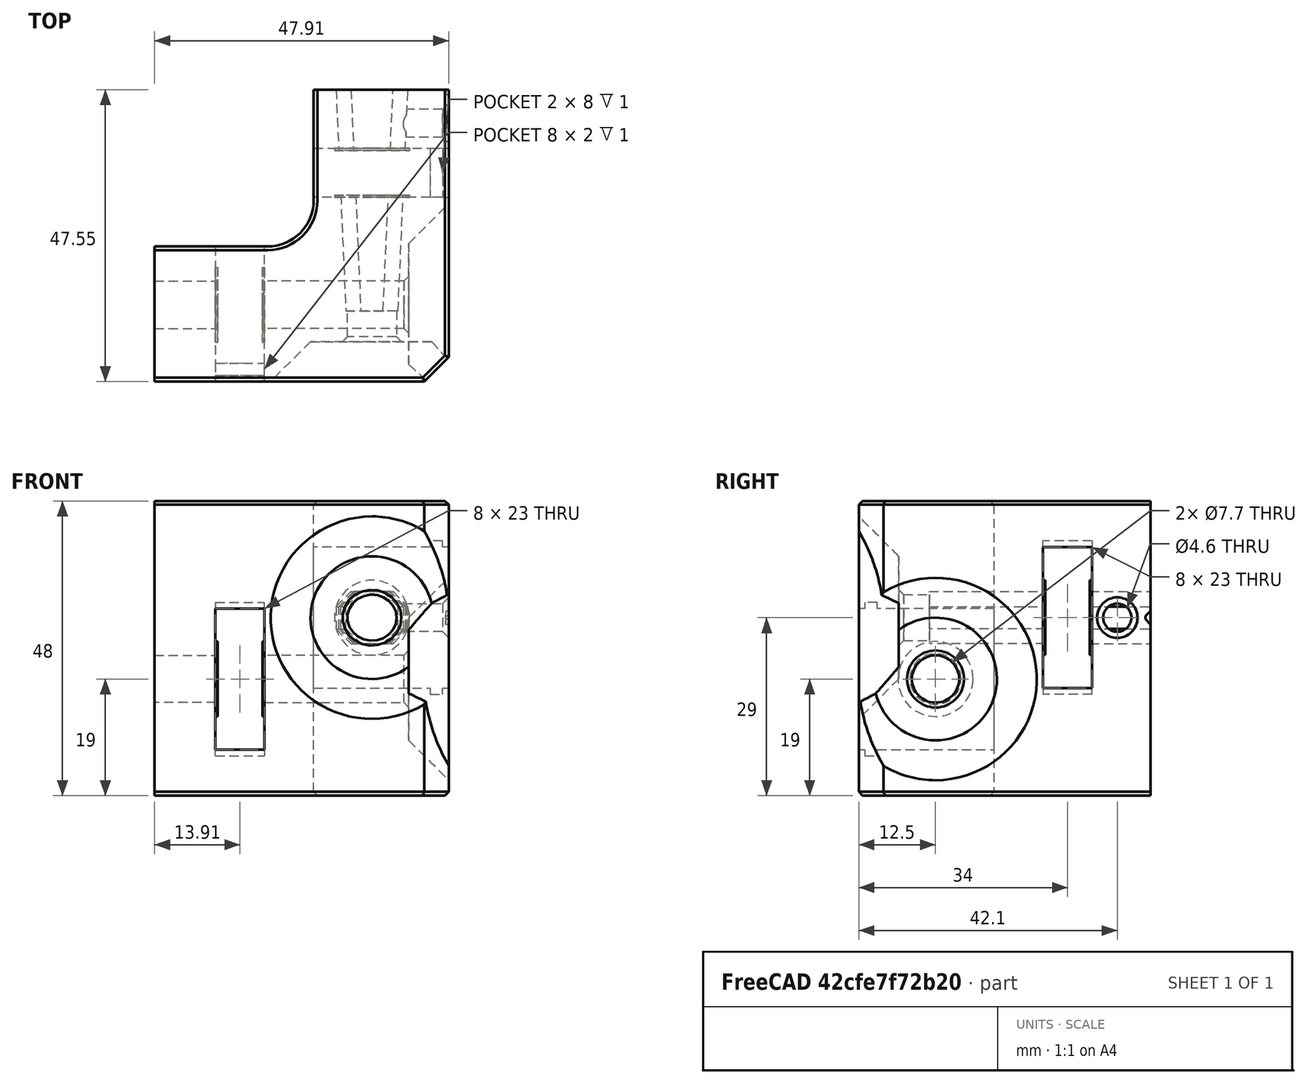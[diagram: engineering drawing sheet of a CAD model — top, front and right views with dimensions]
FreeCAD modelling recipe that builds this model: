
FCSTD DOCUMENT  (FreeCAD 1.0R38641 +678 (Git))
Label: Testpiece_from _60mmx40mm_tube_version
License: All rights reserved
LicenseURL: https://en.wikipedia.org/wiki/All_rights_reserved
objects: Part::Feature×1, PartDesign::FeatureBase×1, Sketcher::SketchObject×1, PartDesign::Pocket×1, PartDesign::Body×1
note: 9 computed .brp shape members not serialized (recipe doc carries the construction recipe); baked Part::Feature solids carry a one-line shape summary decoded from their .brp

FEATURE [Part::Feature] Cut003  label="Bearing ring - with all booleans001"
  shape: bbox 48 x 94.54 x 114.1 mm, 320 faces (baked)
FEATURE [PartDesign::FeatureBase] BaseFeature
  BaseFeature = -> Cut003
  Suppressed = false
FEATURE [Sketcher::SketchObject] Sketch
  ArcFitTolerance = 1e-06
  AttachmentSupport = -> [YZ_Plane]
  FullyConstrained = false
  MakeInternals = false
  MapMode = 5
  Placement = pos=(0,0,0) rot=(0.57735,0.57735,0.57735;2.0944rad)
  sketch-geometry (6):
    g0: LineSegment StartX=-52.603 StartY=-5.59485 StartZ=0 EndX=4.0497 EndY=-5.59485 EndZ=0
    g1: LineSegment StartX=4.0497 StartY=-5.59485 StartZ=0 EndX=4.0497 EndY=-63.1029 EndZ=0
    g2: LineSegment StartX=4.0497 StartY=-63.1029 StartZ=0 EndX=82.855 EndY=-63.1029 EndZ=0
    g3: LineSegment StartX=82.855 StartY=-63.1029 StartZ=0 EndX=76.1628 EndY=73.3227 EndZ=0
    g4: LineSegment StartX=76.1628 StartY=73.3227 StartZ=0 EndX=-61.6335 EndY=67.6786 EndZ=0
    g5: LineSegment StartX=-61.6335 StartY=67.6786 StartZ=0 EndX=-52.603 EndY=-5.59485 EndZ=0
  constraints (9):
    c: Horizontal(g0)
    c: Coincident(g0,g1)
    c: Vertical(g1)
    c: Coincident(g1,g2)
    c: Horizontal(g2)
    c: Coincident(g2,g3)
    c: Coincident(g3,g4)
    c: Coincident(g4,g5)
    c: Coincident(g5,g0)
FEATURE [PartDesign::Pocket] Pocket
  BaseFeature = -> BaseFeature
  Direction = (-1,0,0)
  Length = 5
  Length2 = 5
  Midplane = true
  Profile = -> Sketch
  ReferenceAxis = -> Sketch [N_Axis]
  Refine = true
  Suppressed = false
  Type = 1
FEATURE [PartDesign::Body] Body  label="Testpiece"
  AllowCompound = false
  BaseFeature = -> Cut003
  Group = -> [BaseFeature,Sketch,Pocket]
  Origin = -> Origin
  Placement = pos=(0,0,0) rot=(0,1,0;4.71239rad)
  Tip = -> Pocket
